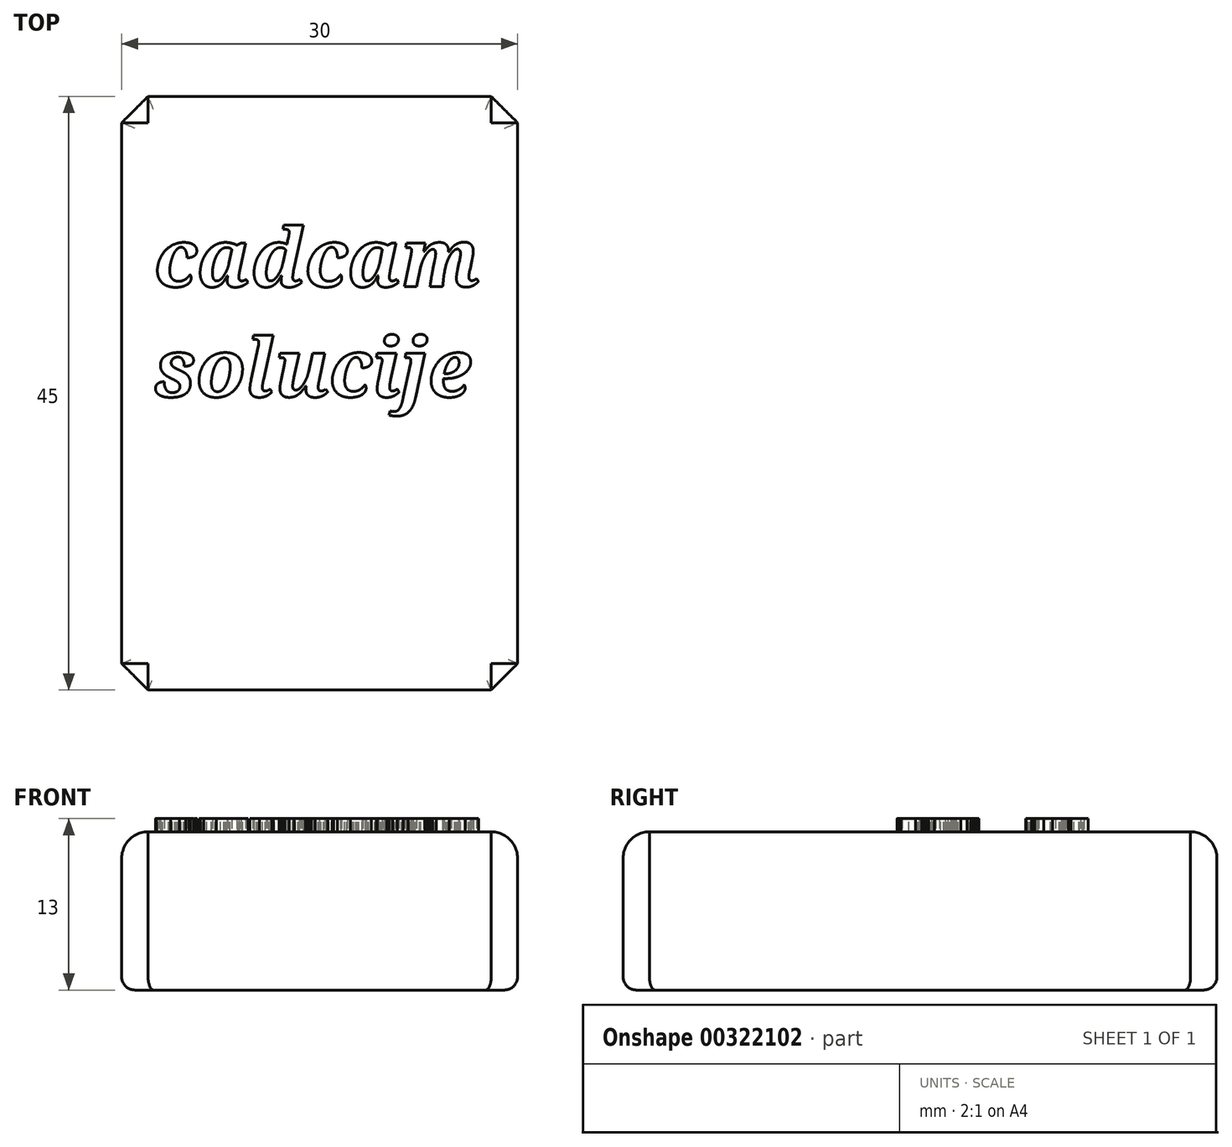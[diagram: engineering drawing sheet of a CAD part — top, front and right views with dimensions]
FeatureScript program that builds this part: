
annotation { "Feature Type Name" : "Feature", "Feature Type Description" : "" }
export const myFeature = defineFeature(function(context is Context, id is Id, definition is map)
    precondition{}
    {
        {
            var Q0;
            Q0=qCreatedBy(makeId("Top.planeOp"),FACE);
            var sketch = newSketch(context, id + "F0", { "sketchPlane" : qUnion([Q0])});
            skLineSegment(sketch, "E0", {"start": v(-25.2, 51.56) * mm, "end": v(-25.2, 96.56) * mm});
            skLineSegment(sketch, "E1", {"start": v(-25.2, 96.56) * mm, "end": v(4.8, 96.56) * mm});
            skLineSegment(sketch, "E2", {"start": v(4.8, 96.56) * mm, "end": v(4.8, 51.56) * mm});
            skLineSegment(sketch, "E3", {"start": v(-25.2, 51.56) * mm, "end": v(4.8, 51.56) * mm});
            skSolve(sketch);
        }
        {
            var Q0;
            Q0 = qSketchRegion(id + "F0", true);
            extrude(context, id + "F1", {"entities" : qUnion([Q0]), "depth" : 12 * mm});
        }
        {
            var Q0;
            Q0=makeQuery(id+"F1.opExtrude","CAP_FACE",FACE,{"disambiguationData":[OSD([sQuery(id+"F0.wireOp",EDGE,"E0"),sQuery(id+"F0.wireOp",EDGE,"E1"),sQuery(id+"F0.wireOp",EDGE,"E2"),sQuery(id+"F0.wireOp",EDGE,"E3")])],"isStart":false});
            fillet(context, id + "F2", {"entities" : qUnion([Q0]), "radius" : 2 * mm, "tangentPropagation" : true, "allowEdgeOverflow" : false});
        }
        {
            var Q0;
            Q0=makeQuery(id+"F1.opExtrude","SWEPT_EDGE",EDGE,{"disambiguationData":[OSD([sQuery(id+"F0.wireOp",EDGE,"E2"),sQuery(id+"F0.wireOp",EDGE,"E3")])]});
            var Q1;
            Q1=makeQuery(id+"F1.opExtrude","SWEPT_EDGE",EDGE,{"disambiguationData":[OSD([sQuery(id+"F0.wireOp",EDGE,"E0"),sQuery(id+"F0.wireOp",EDGE,"E3")])]});
            var Q2;
            Q2=makeQuery(id+"F1.opExtrude","SWEPT_EDGE",EDGE,{"disambiguationData":[OSD([sQuery(id+"F0.wireOp",EDGE,"E1"),sQuery(id+"F0.wireOp",EDGE,"E2")])]});
            var Q3;
            Q3=makeQuery(id+"F1.opExtrude","SWEPT_EDGE",EDGE,{"disambiguationData":[OSD([sQuery(id+"F0.wireOp",EDGE,"E0"),sQuery(id+"F0.wireOp",EDGE,"E1")])]});
            chamfer(context, id + "F3", {"entities" : qUnion([Q0, Q1, Q2, Q3]), "width" : 2 * mm, "tangentPropagation" : true});
        }
        {
            var Q0;
            Q0=makeQuery(id+"F1.opExtrude","CAP_FACE",FACE,{"disambiguationData":[OSD([sQuery(id+"F0.wireOp",EDGE,"E0"),sQuery(id+"F0.wireOp",EDGE,"E1"),sQuery(id+"F0.wireOp",EDGE,"E2"),sQuery(id+"F0.wireOp",EDGE,"E3")])],"isStart":true});
            fillet(context, id + "F4", {"entities" : qUnion([Q0]), "radius" : 1 * mm, "tangentPropagation" : true, "allowEdgeOverflow" : false});
        }
        {
            var Q0;
            Q0=qCreatedBy(makeId("Top.planeOp"),FACE);
            var sketch = newSketch(context, id + "F5", { "sketchPlane" : qUnion([Q0])});
            skText(sketch, "E4", { "text": "cadcam\nsolucije\n", "fontName": "NotoSerif-BoldItalic.ttf"});
            const initialGuessF5  = {"E4": [-0.02275, 0.08214, 1, 0, 0.00442]};
            skSetInitialGuess(sketch, initialGuessF5);
            skSolve(sketch);
        }
        {
            var Q0;
            Q0 = qSketchRegion(id + "F5", true);
            extrude(context, id + "F6", {"entities" : qUnion([Q0]), "operationType" : NewBodyOperationType.ADD, "depth" : 13 * mm});
        }
    });
